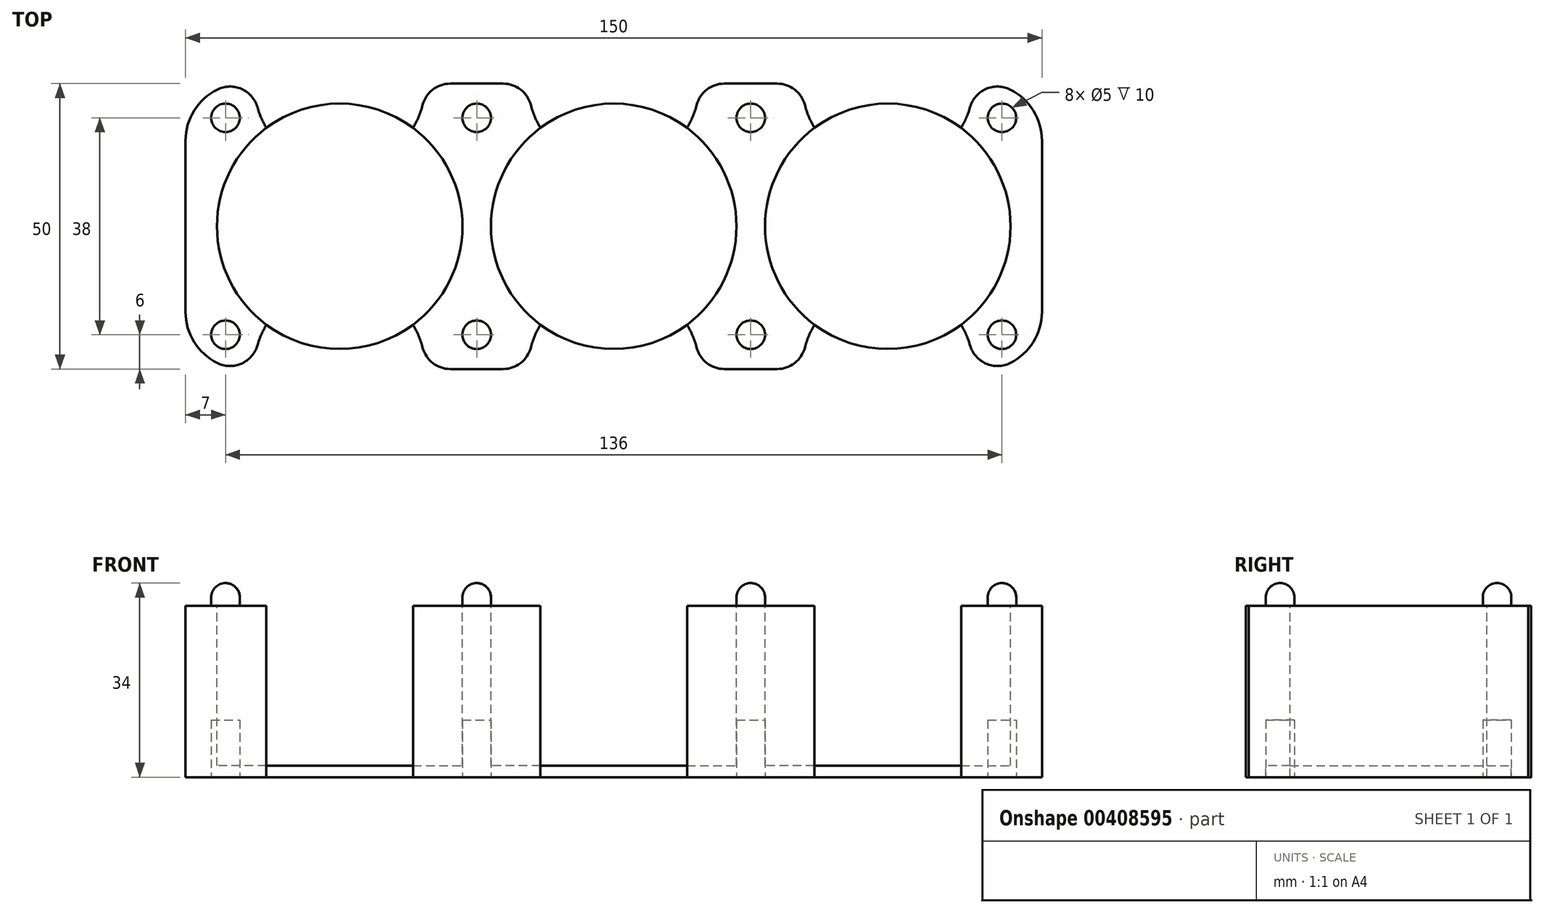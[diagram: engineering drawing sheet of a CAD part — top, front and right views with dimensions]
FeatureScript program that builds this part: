
annotation { "Feature Type Name" : "Feature", "Feature Type Description" : "" }
export const myFeature = defineFeature(function(context is Context, id is Id, definition is map)
    precondition{}
    {
        {
            var Q0;
            Q0=qCreatedBy(makeId("Top.planeOp"),FACE);
            var sketch = newSketch(context, id + "F0", { "sketchPlane" : qUnion([Q0])});
            skLineSegment(sketch, "E0.bottom", {"start": v(0, 0) * mm, "end": v(150, 0) * mm});
            skLineSegment(sketch, "E0.top", {"start": v(0, 50) * mm, "end": v(150, 50) * mm});
            skLineSegment(sketch, "E0.left", {"start": v(0, 0) * mm, "end": v(0, 50) * mm});
            skLineSegment(sketch, "E0.right", {"start": v(150, 0) * mm, "end": v(150, 50) * mm});
            skSolve(sketch);
        }
        {
            var Q0;
            Q0=makeQuery(id+"F0.imprint","IMPRINT",FACE,{"disambiguationData":[TD([[makeQuery(id+"F0.imprint","IMPRINT",EDGE,{"derivedFrom":sQuery(id+"F0.wireOp",EDGE,"E0.bottom")}),1.0]])]});
            var Q1;
            Q1 = qSketchRegion(id + "F2", true);
            extrude(context, id + "F1", {"entities" : qUnion([Q0, Q1]), "depth" : 30 * mm});
        }
        {
            var Q0;
            Q0=makeQuery(id+"F1.opExtrude","CAP_FACE",FACE,{"disambiguationData":[OSD([sQuery(id+"F0.wireOp",EDGE,"E0.bottom"),sQuery(id+"F0.wireOp",EDGE,"E0.top"),sQuery(id+"F0.wireOp",EDGE,"E0.left"),sQuery(id+"F0.wireOp",EDGE,"E0.right")])],"isStart":false});
            var sketch = newSketch(context, id + "F2", { "sketchPlane" : qUnion([Q0])});
            skCircle(sketch, "E1", {"center": v(27, 25) * mm, "radius": 21.5 * mm});
            skCircle(sketch, "E2", {"center": v(75, 25) * mm, "radius": 21.5 * mm});
            skCircle(sketch, "E3", {"center": v(123, 25) * mm, "radius": 21.5 * mm});
            skSolve(sketch);
        }
        {
            var Q0;
            Q0=makeQuery(id+"F2.imprint","IMPRINT",FACE,{"disambiguationData":[TD([[makeQuery(id+"F2.imprint","IMPRINT",EDGE,{"derivedFrom":sQuery(id+"F2.wireOp",EDGE,"E2")}),1.0]])]});
            var Q1;
            Q1=makeQuery(id+"F2.imprint","IMPRINT",FACE,{"disambiguationData":[TD([[makeQuery(id+"F2.imprint","IMPRINT",EDGE,{"derivedFrom":sQuery(id+"F2.wireOp",EDGE,"E3")}),1.0]])]});
            var Q2;
            Q2=makeQuery(id+"F2.imprint","IMPRINT",FACE,{"disambiguationData":[TD([[makeQuery(id+"F2.imprint","IMPRINT",EDGE,{"derivedFrom":sQuery(id+"F2.wireOp",EDGE,"E1")}),1.0]])]});
            extrude(context, id + "F3", {"entities" : qUnion([Q0, Q1, Q2]), "operationType" : NewBodyOperationType.REMOVE, "oppositeDirection" : true, "depth" : 28 * mm});
        }
        {
            var Q0;
            Q0=makeQuery(id+"F1.opExtrude","CAP_FACE",FACE,{"disambiguationData":[OSD([sQuery(id+"F0.wireOp",EDGE,"E0.bottom"),sQuery(id+"F0.wireOp",EDGE,"E0.top"),sQuery(id+"F0.wireOp",EDGE,"E0.left"),sQuery(id+"F0.wireOp",EDGE,"E0.right")])],"isStart":false});
            var sketch = newSketch(context, id + "F4", { "sketchPlane" : qUnion([Q0])});
            skCircle(sketch, "E4", {"center": v(75, 50) * mm, "radius": 15 * mm});
            skCircle(sketch, "E5", {"center": v(123, 50) * mm, "radius": 15 * mm});
            skCircle(sketch, "E6", {"center": v(27, 50) * mm, "radius": 15 * mm});
            skCircle(sketch, "E7", {"center": v(27, 0) * mm, "radius": 15 * mm});
            skCircle(sketch, "E8", {"center": v(75, 0) * mm, "radius": 15 * mm});
            skCircle(sketch, "E9", {"center": v(123, 0) * mm, "radius": 15 * mm});
            skSolve(sketch);
        }
        {
            var Q0;
            {var subQ0=sQuery(id+"F4.wireOp",EDGE,"E4");var subQ1=makeQuery(id+"F1.opExtrude","CAP_EDGE",EDGE,{"disambiguationData":[OSD([sQuery(id+"F0.wireOp",EDGE,"E0.top")])],"isStart":false});var subQ2=makeQuery(id+"F4.imprint","INTERSECT",VERTEX,{"disambiguationData":[OD(0.0)],"derivedFrom":[subQ1,subQ0]});Q0=makeQuery(id+"F4.imprint","IMPRINT",FACE,{"disambiguationData":[TD([[makeQuery(id+"F4.imprint","IMPRINT",EDGE,{"disambiguationData":[TD([[subQ2,1.0]])],"derivedFrom":subQ0}),1.0]])]});}
            var Q1;
            {var subQ0=sQuery(id+"F4.wireOp",EDGE,"E5");var subQ1=makeQuery(id+"F1.opExtrude","CAP_EDGE",EDGE,{"disambiguationData":[OSD([sQuery(id+"F0.wireOp",EDGE,"E0.top")])],"isStart":false});var subQ2=makeQuery(id+"F4.imprint","INTERSECT",VERTEX,{"disambiguationData":[OD(0.0)],"derivedFrom":[subQ1,subQ0]});Q1=makeQuery(id+"F4.imprint","IMPRINT",FACE,{"disambiguationData":[TD([[makeQuery(id+"F4.imprint","IMPRINT",EDGE,{"disambiguationData":[TD([[subQ2,1.0]])],"derivedFrom":subQ0}),1.0]])]});}
            var Q2;
            {var subQ0=sQuery(id+"F4.wireOp",EDGE,"E7");var subQ1=makeQuery(id+"F1.opExtrude","CAP_EDGE",EDGE,{"disambiguationData":[OSD([sQuery(id+"F0.wireOp",EDGE,"E0.bottom")])],"isStart":false});var subQ2=makeQuery(id+"F4.imprint","INTERSECT",VERTEX,{"disambiguationData":[OD(0.0)],"derivedFrom":[subQ1,subQ0]});Q2=makeQuery(id+"F4.imprint","IMPRINT",FACE,{"disambiguationData":[TD([[makeQuery(id+"F4.imprint","IMPRINT",EDGE,{"disambiguationData":[TD([[subQ2,1.0]])],"derivedFrom":subQ0}),1.0]])]});}
            var Q3;
            {var subQ0=sQuery(id+"F4.wireOp",EDGE,"E8");var subQ1=makeQuery(id+"F1.opExtrude","CAP_EDGE",EDGE,{"disambiguationData":[OSD([sQuery(id+"F0.wireOp",EDGE,"E0.bottom")])],"isStart":false});var subQ2=makeQuery(id+"F4.imprint","INTERSECT",VERTEX,{"disambiguationData":[OD(0.0)],"derivedFrom":[subQ1,subQ0]});Q3=makeQuery(id+"F4.imprint","IMPRINT",FACE,{"disambiguationData":[TD([[makeQuery(id+"F4.imprint","IMPRINT",EDGE,{"disambiguationData":[TD([[subQ2,1.0]])],"derivedFrom":subQ0}),1.0]])]});}
            var Q4;
            {var subQ0=sQuery(id+"F4.wireOp",EDGE,"E9");var subQ1=makeQuery(id+"F1.opExtrude","CAP_EDGE",EDGE,{"disambiguationData":[OSD([sQuery(id+"F0.wireOp",EDGE,"E0.bottom")])],"isStart":false});var subQ2=makeQuery(id+"F4.imprint","INTERSECT",VERTEX,{"disambiguationData":[OD(0.0)],"derivedFrom":[subQ1,subQ0]});Q4=makeQuery(id+"F4.imprint","IMPRINT",FACE,{"disambiguationData":[TD([[makeQuery(id+"F4.imprint","IMPRINT",EDGE,{"disambiguationData":[TD([[subQ2,1.0]])],"derivedFrom":subQ0}),1.0]])]});}
            var Q5;
            {var subQ0=sQuery(id+"F4.wireOp",EDGE,"E4");var subQ1=makeQuery(id+"F3.boolean.opBoolean","COPY",EDGE,{"derivedFrom":makeQuery(id+"F3.opExtrude","CAP_EDGE",EDGE,{"disambiguationData":[OSD([sQuery(id+"F2.wireOp",EDGE,"E2")])],"isStart":true})});var subQ2=makeQuery(id+"F4.imprint","INTERSECT",VERTEX,{"disambiguationData":[OD(0.0)],"derivedFrom":[subQ1,subQ0]});Q5=makeQuery(id+"F4.imprint","IMPRINT",FACE,{"disambiguationData":[TD([[makeQuery(id+"F4.imprint","IMPRINT",EDGE,{"disambiguationData":[TD([[subQ2,-1.0]])],"derivedFrom":subQ0}),1.0]])]});}
            var Q6;
            {var subQ0=sQuery(id+"F4.wireOp",EDGE,"E5");var subQ1=makeQuery(id+"F3.boolean.opBoolean","COPY",EDGE,{"derivedFrom":makeQuery(id+"F3.opExtrude","CAP_EDGE",EDGE,{"disambiguationData":[OSD([sQuery(id+"F2.wireOp",EDGE,"E3")])],"isStart":true})});var subQ2=makeQuery(id+"F4.imprint","INTERSECT",VERTEX,{"disambiguationData":[OD(0.0)],"derivedFrom":[subQ1,subQ0]});Q6=makeQuery(id+"F4.imprint","IMPRINT",FACE,{"disambiguationData":[TD([[makeQuery(id+"F4.imprint","IMPRINT",EDGE,{"disambiguationData":[TD([[subQ2,-1.0]])],"derivedFrom":subQ0}),1.0]])]});}
            var Q7;
            {var subQ0=sQuery(id+"F4.wireOp",EDGE,"E6");var subQ1=makeQuery(id+"F3.boolean.opBoolean","COPY",EDGE,{"derivedFrom":makeQuery(id+"F3.opExtrude","CAP_EDGE",EDGE,{"disambiguationData":[OSD([sQuery(id+"F2.wireOp",EDGE,"E1")])],"isStart":true})});var subQ2=makeQuery(id+"F4.imprint","INTERSECT",VERTEX,{"disambiguationData":[OD(0.0)],"derivedFrom":[subQ1,subQ0]});Q7=makeQuery(id+"F4.imprint","IMPRINT",FACE,{"disambiguationData":[TD([[makeQuery(id+"F4.imprint","IMPRINT",EDGE,{"disambiguationData":[TD([[subQ2,-1.0]])],"derivedFrom":subQ0}),1.0]])]});}
            var Q8;
            {var subQ0=sQuery(id+"F4.wireOp",EDGE,"E7");var subQ1=makeQuery(id+"F3.boolean.opBoolean","COPY",EDGE,{"derivedFrom":makeQuery(id+"F3.opExtrude","CAP_EDGE",EDGE,{"disambiguationData":[OSD([sQuery(id+"F2.wireOp",EDGE,"E1")])],"isStart":true})});var subQ2=makeQuery(id+"F4.imprint","INTERSECT",VERTEX,{"disambiguationData":[OD(0.0)],"derivedFrom":[subQ1,subQ0]});Q8=makeQuery(id+"F4.imprint","IMPRINT",FACE,{"disambiguationData":[TD([[makeQuery(id+"F4.imprint","IMPRINT",EDGE,{"disambiguationData":[TD([[subQ2,-1.0]])],"derivedFrom":subQ0}),1.0]])]});}
            var Q9;
            {var subQ0=sQuery(id+"F4.wireOp",EDGE,"E8");var subQ1=makeQuery(id+"F3.boolean.opBoolean","COPY",EDGE,{"derivedFrom":makeQuery(id+"F3.opExtrude","CAP_EDGE",EDGE,{"disambiguationData":[OSD([sQuery(id+"F2.wireOp",EDGE,"E2")])],"isStart":true})});var subQ2=makeQuery(id+"F4.imprint","INTERSECT",VERTEX,{"disambiguationData":[OD(0.0)],"derivedFrom":[subQ1,subQ0]});Q9=makeQuery(id+"F4.imprint","IMPRINT",FACE,{"disambiguationData":[TD([[makeQuery(id+"F4.imprint","IMPRINT",EDGE,{"disambiguationData":[TD([[subQ2,-1.0]])],"derivedFrom":subQ0}),1.0]])]});}
            var Q10;
            {var subQ0=sQuery(id+"F4.wireOp",EDGE,"E9");var subQ1=makeQuery(id+"F3.boolean.opBoolean","COPY",EDGE,{"derivedFrom":makeQuery(id+"F3.opExtrude","CAP_EDGE",EDGE,{"disambiguationData":[OSD([sQuery(id+"F2.wireOp",EDGE,"E3")])],"isStart":true})});var subQ2=makeQuery(id+"F4.imprint","INTERSECT",VERTEX,{"disambiguationData":[OD(0.0)],"derivedFrom":[subQ1,subQ0]});Q10=makeQuery(id+"F4.imprint","IMPRINT",FACE,{"disambiguationData":[TD([[makeQuery(id+"F4.imprint","IMPRINT",EDGE,{"disambiguationData":[TD([[subQ2,-1.0]])],"derivedFrom":subQ0}),1.0]])]});}
            var Q11;
            {var subQ0=sQuery(id+"F4.wireOp",EDGE,"E4");var subQ1=makeQuery(id+"F1.opExtrude","CAP_EDGE",EDGE,{"disambiguationData":[OSD([sQuery(id+"F0.wireOp",EDGE,"E0.top")])],"isStart":false});var subQ2=makeQuery(id+"F4.imprint","INTERSECT",VERTEX,{"disambiguationData":[OD(0.0)],"derivedFrom":[subQ1,subQ0]});Q11=makeQuery(id+"F4.imprint","IMPRINT",FACE,{"disambiguationData":[TD([[makeQuery(id+"F4.imprint","IMPRINT",EDGE,{"disambiguationData":[TD([[subQ2,-1.0]])],"derivedFrom":subQ0}),1.0]])]});}
            var Q12;
            {var subQ0=sQuery(id+"F4.wireOp",EDGE,"E5");var subQ1=makeQuery(id+"F1.opExtrude","CAP_EDGE",EDGE,{"disambiguationData":[OSD([sQuery(id+"F0.wireOp",EDGE,"E0.top")])],"isStart":false});var subQ2=makeQuery(id+"F4.imprint","INTERSECT",VERTEX,{"disambiguationData":[OD(0.0)],"derivedFrom":[subQ1,subQ0]});Q12=makeQuery(id+"F4.imprint","IMPRINT",FACE,{"disambiguationData":[TD([[makeQuery(id+"F4.imprint","IMPRINT",EDGE,{"disambiguationData":[TD([[subQ2,-1.0]])],"derivedFrom":subQ0}),1.0]])]});}
            var Q13;
            {var subQ0=sQuery(id+"F4.wireOp",EDGE,"E6");var subQ1=makeQuery(id+"F1.opExtrude","CAP_EDGE",EDGE,{"disambiguationData":[OSD([sQuery(id+"F0.wireOp",EDGE,"E0.top")])],"isStart":false});var subQ2=makeQuery(id+"F4.imprint","INTERSECT",VERTEX,{"disambiguationData":[OD(0.0)],"derivedFrom":[subQ1,subQ0]});Q13=makeQuery(id+"F4.imprint","IMPRINT",FACE,{"disambiguationData":[TD([[makeQuery(id+"F4.imprint","IMPRINT",EDGE,{"disambiguationData":[TD([[subQ2,-1.0]])],"derivedFrom":subQ0}),1.0]])]});}
            var Q14;
            {var subQ0=sQuery(id+"F4.wireOp",EDGE,"E7");var subQ1=makeQuery(id+"F1.opExtrude","CAP_EDGE",EDGE,{"disambiguationData":[OSD([sQuery(id+"F0.wireOp",EDGE,"E0.bottom")])],"isStart":false});var subQ2=makeQuery(id+"F4.imprint","INTERSECT",VERTEX,{"disambiguationData":[OD(0.0)],"derivedFrom":[subQ1,subQ0]});Q14=makeQuery(id+"F4.imprint","IMPRINT",FACE,{"disambiguationData":[TD([[makeQuery(id+"F4.imprint","IMPRINT",EDGE,{"disambiguationData":[TD([[subQ2,-1.0]])],"derivedFrom":subQ0}),1.0]])]});}
            var Q15;
            {var subQ0=sQuery(id+"F4.wireOp",EDGE,"E8");var subQ1=makeQuery(id+"F1.opExtrude","CAP_EDGE",EDGE,{"disambiguationData":[OSD([sQuery(id+"F0.wireOp",EDGE,"E0.bottom")])],"isStart":false});var subQ2=makeQuery(id+"F4.imprint","INTERSECT",VERTEX,{"disambiguationData":[OD(0.0)],"derivedFrom":[subQ1,subQ0]});Q15=makeQuery(id+"F4.imprint","IMPRINT",FACE,{"disambiguationData":[TD([[makeQuery(id+"F4.imprint","IMPRINT",EDGE,{"disambiguationData":[TD([[subQ2,-1.0]])],"derivedFrom":subQ0}),1.0]])]});}
            var Q16;
            {var subQ0=sQuery(id+"F4.wireOp",EDGE,"E9");var subQ1=makeQuery(id+"F1.opExtrude","CAP_EDGE",EDGE,{"disambiguationData":[OSD([sQuery(id+"F0.wireOp",EDGE,"E0.bottom")])],"isStart":false});var subQ2=makeQuery(id+"F4.imprint","INTERSECT",VERTEX,{"disambiguationData":[OD(0.0)],"derivedFrom":[subQ1,subQ0]});Q16=makeQuery(id+"F4.imprint","IMPRINT",FACE,{"disambiguationData":[TD([[makeQuery(id+"F4.imprint","IMPRINT",EDGE,{"disambiguationData":[TD([[subQ2,-1.0]])],"derivedFrom":subQ0}),1.0]])]});}
            extrude(context, id + "F5", {"entities" : qUnion([Q0, Q1, Q2, Q3, Q4, Q5, Q6, Q7, Q8, Q9, Q10, Q11, Q12, Q13, Q14, Q15, Q16]), "operationType" : NewBodyOperationType.REMOVE, "endBound" : BoundingType.THROUGH_ALL, "oppositeDirection" : true, "depth" : 25 * mm});
        }
        {
            var Q0;
            Q0=makeQuery(id+"F1.opExtrude","SWEPT_EDGE",EDGE,{"disambiguationData":[OSD([sQuery(id+"F0.wireOp",EDGE,"E0.bottom"),sQuery(id+"F0.wireOp",EDGE,"E0.right")])]});
            fillet(context, id + "F6", {"entities" : qUnion([Q0]), "radius" : 10 * mm, "tangentPropagation" : true, "allowEdgeOverflow" : false});
        }
        {
            var Q0;
            Q0=makeQuery(id+"F1.opExtrude","SWEPT_EDGE",EDGE,{"disambiguationData":[OSD([sQuery(id+"F0.wireOp",EDGE,"E0.top"),sQuery(id+"F0.wireOp",EDGE,"E0.right")])]});
            var Q1;
            Q1=makeQuery(id+"F1.opExtrude","SWEPT_EDGE",EDGE,{"disambiguationData":[OSD([sQuery(id+"F0.wireOp",EDGE,"E0.bottom"),sQuery(id+"F0.wireOp",EDGE,"E0.left")])]});
            var Q2;
            Q2=makeQuery(id+"F1.opExtrude","SWEPT_EDGE",EDGE,{"disambiguationData":[OSD([sQuery(id+"F0.wireOp",EDGE,"E0.top"),sQuery(id+"F0.wireOp",EDGE,"E0.left")])]});
            fillet(context, id + "F7", {"entities" : qUnion([Q0, Q1, Q2]), "radius" : 10 * mm, "tangentPropagation" : true, "allowEdgeOverflow" : false});
        }
        {
            var Q0;
            Q0=makeQuery(id+"F5.boolean.opBoolean","INTERSECT",EDGE,{"disambiguationData":[OD(0.0)],"derivedFrom":[makeQuery(id+"F1.opExtrude","SWEPT_FACE",FACE,{"disambiguationData":[OSD([sQuery(id+"F0.wireOp",EDGE,"E0.bottom")])]}),makeQuery(id+"F5.opExtrude","SWEPT_FACE",FACE,{"disambiguationData":[OSD([sQuery(id+"F4.wireOp",EDGE,"E7")])]})]});
            var Q1;
            {var subQ0=sQuery(id+"F4.wireOp",EDGE,"E6");var subQ1=sQuery(id+"F0.wireOp",EDGE,"E0.top");Q1=makeQuery(id+"F5.boolean.opBoolean","COPY",EDGE,{"derivedFrom":makeQuery(id+"F5.opExtrude","SWEPT_EDGE",EDGE,{"disambiguationData":[OSD([subQ1,subQ0]),TDD([makeQuery(id+"F4.imprint","INTERSECT",VERTEX,{"disambiguationData":[OD(0.0)],"derivedFrom":[makeQuery(id+"F1.opExtrude","CAP_EDGE",EDGE,{"disambiguationData":[OSD([subQ1])],"isStart":false}),subQ0]})])]})});}
            var Q2;
            Q2=makeQuery(id+"F5.boolean.opBoolean","INTERSECT",EDGE,{"disambiguationData":[OD(0.0)],"derivedFrom":[makeQuery(id+"F1.opExtrude","SWEPT_FACE",FACE,{"disambiguationData":[OSD([sQuery(id+"F0.wireOp",EDGE,"E0.top")])]}),makeQuery(id+"F5.opExtrude","SWEPT_FACE",FACE,{"disambiguationData":[OSD([sQuery(id+"F4.wireOp",EDGE,"E4")])]})]});
            var Q3;
            Q3=makeQuery(id+"F5.boolean.opBoolean","INTERSECT",EDGE,{"disambiguationData":[OD(1.0)],"derivedFrom":[makeQuery(id+"F1.opExtrude","SWEPT_FACE",FACE,{"disambiguationData":[OSD([sQuery(id+"F0.wireOp",EDGE,"E0.top")])]}),makeQuery(id+"F5.opExtrude","SWEPT_FACE",FACE,{"disambiguationData":[OSD([sQuery(id+"F4.wireOp",EDGE,"E5")])]})]});
            var Q4;
            Q4=makeQuery(id+"F5.boolean.opBoolean","INTERSECT",EDGE,{"disambiguationData":[OD(1.0)],"derivedFrom":[makeQuery(id+"F1.opExtrude","SWEPT_FACE",FACE,{"disambiguationData":[OSD([sQuery(id+"F0.wireOp",EDGE,"E0.bottom")])]}),makeQuery(id+"F5.opExtrude","SWEPT_FACE",FACE,{"disambiguationData":[OSD([sQuery(id+"F4.wireOp",EDGE,"E9")])]})]});
            var Q5;
            Q5=makeQuery(id+"F5.boolean.opBoolean","INTERSECT",EDGE,{"disambiguationData":[OD(1.0)],"derivedFrom":[makeQuery(id+"F1.opExtrude","SWEPT_FACE",FACE,{"disambiguationData":[OSD([sQuery(id+"F0.wireOp",EDGE,"E0.bottom")])]}),makeQuery(id+"F5.opExtrude","SWEPT_FACE",FACE,{"disambiguationData":[OSD([sQuery(id+"F4.wireOp",EDGE,"E8")])]})]});
            var Q6;
            Q6=makeQuery(id+"F5.boolean.opBoolean","INTERSECT",EDGE,{"disambiguationData":[OD(1.0)],"derivedFrom":[makeQuery(id+"F1.opExtrude","SWEPT_FACE",FACE,{"disambiguationData":[OSD([sQuery(id+"F0.wireOp",EDGE,"E0.bottom")])]}),makeQuery(id+"F5.opExtrude","SWEPT_FACE",FACE,{"disambiguationData":[OSD([sQuery(id+"F4.wireOp",EDGE,"E7")])]})]});
            var Q7;
            Q7=makeQuery(id+"F5.boolean.opBoolean","INTERSECT",EDGE,{"disambiguationData":[OD(0.0)],"derivedFrom":[makeQuery(id+"F1.opExtrude","SWEPT_FACE",FACE,{"disambiguationData":[OSD([sQuery(id+"F0.wireOp",EDGE,"E0.bottom")])]}),makeQuery(id+"F5.opExtrude","SWEPT_FACE",FACE,{"disambiguationData":[OSD([sQuery(id+"F4.wireOp",EDGE,"E8")])]})]});
            var Q8;
            Q8=makeQuery(id+"F5.boolean.opBoolean","INTERSECT",EDGE,{"disambiguationData":[OD(0.0)],"derivedFrom":[makeQuery(id+"F1.opExtrude","SWEPT_FACE",FACE,{"disambiguationData":[OSD([sQuery(id+"F0.wireOp",EDGE,"E0.bottom")])]}),makeQuery(id+"F5.opExtrude","SWEPT_FACE",FACE,{"disambiguationData":[OSD([sQuery(id+"F4.wireOp",EDGE,"E9")])]})]});
            var Q9;
            {var subQ0=sQuery(id+"F4.wireOp",EDGE,"E6");var subQ1=sQuery(id+"F0.wireOp",EDGE,"E0.top");Q9=makeQuery(id+"F5.boolean.opBoolean","COPY",EDGE,{"derivedFrom":makeQuery(id+"F5.opExtrude","SWEPT_EDGE",EDGE,{"disambiguationData":[OSD([subQ1,subQ0]),TDD([makeQuery(id+"F4.imprint","INTERSECT",VERTEX,{"disambiguationData":[OD(1.0)],"derivedFrom":[makeQuery(id+"F1.opExtrude","CAP_EDGE",EDGE,{"disambiguationData":[OSD([subQ1])],"isStart":false}),subQ0]})])]})});}
            var Q10;
            Q10=makeQuery(id+"F5.boolean.opBoolean","INTERSECT",EDGE,{"disambiguationData":[OD(1.0)],"derivedFrom":[makeQuery(id+"F1.opExtrude","SWEPT_FACE",FACE,{"disambiguationData":[OSD([sQuery(id+"F0.wireOp",EDGE,"E0.top")])]}),makeQuery(id+"F5.opExtrude","SWEPT_FACE",FACE,{"disambiguationData":[OSD([sQuery(id+"F4.wireOp",EDGE,"E4")])]})]});
            var Q11;
            Q11=makeQuery(id+"F5.boolean.opBoolean","INTERSECT",EDGE,{"disambiguationData":[OD(0.0)],"derivedFrom":[makeQuery(id+"F1.opExtrude","SWEPT_FACE",FACE,{"disambiguationData":[OSD([sQuery(id+"F0.wireOp",EDGE,"E0.top")])]}),makeQuery(id+"F5.opExtrude","SWEPT_FACE",FACE,{"disambiguationData":[OSD([sQuery(id+"F4.wireOp",EDGE,"E5")])]})]});
            fillet(context, id + "F8", {"entities" : qUnion([Q0, Q1, Q2, Q3, Q4, Q5, Q6, Q7, Q8, Q9, Q10, Q11]), "radius" : 5 * mm, "tangentPropagation" : true, "allowEdgeOverflow" : false});
        }
        {
            var Q0;
            {var subQ0=sQuery(id+"F0.wireOp",EDGE,"E0.bottom");var subQ1=sQuery(id+"F0.wireOp",EDGE,"E0.top");Q0=makeQuery(id+"F5.boolean.opBoolean","SPLIT",FACE,{"disambiguationData":[TD([makeQuery(id+"F1.opExtrude","SWEPT_FACE",FACE,{"disambiguationData":[OSD([subQ0])]}),makeQuery(id+"F1.opExtrude","SWEPT_FACE",FACE,{"disambiguationData":[OSD([subQ1])]}),makeQuery(id+"F3.boolean.opBoolean","COPY",FACE,{"derivedFrom":makeQuery(id+"F3.opExtrude","SWEPT_FACE",FACE,{"disambiguationData":[OSD([sQuery(id+"F2.wireOp",EDGE,"E1")])]})}),makeQuery(id+"F3.boolean.opBoolean","COPY",FACE,{"derivedFrom":makeQuery(id+"F3.opExtrude","SWEPT_FACE",FACE,{"disambiguationData":[OSD([sQuery(id+"F2.wireOp",EDGE,"E2")])]})}),makeQuery(id+"F5.opExtrude","SWEPT_FACE",FACE,{"disambiguationData":[OSD([sQuery(id+"F4.wireOp",EDGE,"E4")])]}),makeQuery(id+"F5.opExtrude","SWEPT_FACE",FACE,{"disambiguationData":[OSD([sQuery(id+"F4.wireOp",EDGE,"E6")])]}),makeQuery(id+"F5.opExtrude","SWEPT_FACE",FACE,{"disambiguationData":[OSD([sQuery(id+"F4.wireOp",EDGE,"E7")])]}),makeQuery(id+"F5.opExtrude","SWEPT_FACE",FACE,{"disambiguationData":[OSD([sQuery(id+"F4.wireOp",EDGE,"E8")])]})])],"derivedFrom":makeQuery(id+"F1.opExtrude","CAP_FACE",FACE,{"disambiguationData":[OSD([subQ0,subQ1,sQuery(id+"F0.wireOp",EDGE,"E0.left"),sQuery(id+"F0.wireOp",EDGE,"E0.right")])],"isStart":false})});}
            var sketch = newSketch(context, id + "F9", { "sketchPlane" : qUnion([Q0])});
            skCircle(sketch, "E10", {"center": v(7, 44) * mm, "radius": 2.5 * mm});
            skCircle(sketch, "E11", {"center": v(51, 44) * mm, "radius": 2.5 * mm});
            skPoint(sketch, "E12.centerSnap0", {"position": v(61.17, 44.19) * mm});
            skCircle(sketch, "E13", {"center": v(143, 44) * mm, "radius": 2.5 * mm});
            skCircle(sketch, "E14", {"center": v(7, 6) * mm, "radius": 2.5 * mm});
            skCircle(sketch, "E15", {"center": v(51, 6) * mm, "radius": 2.5 * mm});
            skCircle(sketch, "E16", {"center": v(99, 6) * mm, "radius": 2.5 * mm});
            skCircle(sketch, "E17", {"center": v(143, 6) * mm, "radius": 2.5 * mm});
            skCircle(sketch, "E18", {"center": v(99, 44) * mm, "radius": 2.5 * mm});
            skSolve(sketch);
        }
        {
            var Q0;
            Q0 = qSketchRegion(id + "F9", true);
            extrude(context, id + "F10", {"entities" : qUnion([Q0]), "operationType" : NewBodyOperationType.ADD, "depth" : 4 * mm});
        }
        {
            var Q0;
            Q0=makeQuery(id+"F10.opExtrude","CAP_EDGE",EDGE,{"disambiguationData":[OSD([sQuery(id+"F9.wireOp",EDGE,"E14")])],"isStart":false});
            var Q1;
            Q1=makeQuery(id+"F10.opExtrude","CAP_EDGE",EDGE,{"disambiguationData":[OSD([sQuery(id+"F9.wireOp",EDGE,"E10")])],"isStart":false});
            var Q2;
            Q2=makeQuery(id+"F10.opExtrude","CAP_EDGE",EDGE,{"disambiguationData":[OSD([sQuery(id+"F9.wireOp",EDGE,"E15")])],"isStart":false});
            var Q3;
            Q3=makeQuery(id+"F10.opExtrude","CAP_EDGE",EDGE,{"disambiguationData":[OSD([sQuery(id+"F9.wireOp",EDGE,"E11")])],"isStart":false});
            var Q4;
            Q4=makeQuery(id+"F10.opExtrude","CAP_EDGE",EDGE,{"disambiguationData":[OSD([sQuery(id+"F9.wireOp",EDGE,"E18")])],"isStart":false});
            var Q5;
            Q5=makeQuery(id+"F10.opExtrude","CAP_EDGE",EDGE,{"disambiguationData":[OSD([sQuery(id+"F9.wireOp",EDGE,"E16")])],"isStart":false});
            var Q6;
            Q6=makeQuery(id+"F10.opExtrude","CAP_EDGE",EDGE,{"disambiguationData":[OSD([sQuery(id+"F9.wireOp",EDGE,"E17")])],"isStart":false});
            var Q7;
            Q7=makeQuery(id+"F10.opExtrude","CAP_EDGE",EDGE,{"disambiguationData":[OSD([sQuery(id+"F9.wireOp",EDGE,"E13")])],"isStart":false});
            fillet(context, id + "F11", {"entities" : qUnion([Q0, Q1, Q2, Q3, Q4, Q5, Q6, Q7]), "radius" : 2.5 * mm, "tangentPropagation" : true, "allowEdgeOverflow" : false});
        }
        {
            var Q0;
            Q0=makeQuery(id+"F1.opExtrude","CAP_FACE",FACE,{"disambiguationData":[OSD([sQuery(id+"F0.wireOp",EDGE,"E0.bottom"),sQuery(id+"F0.wireOp",EDGE,"E0.top"),sQuery(id+"F0.wireOp",EDGE,"E0.left"),sQuery(id+"F0.wireOp",EDGE,"E0.right")])],"isStart":true});
            var sketch = newSketch(context, id + "F12", { "sketchPlane" : qUnion([Q0])});
            skCircle(sketch, "E19", {"center": v(7, -6) * mm, "radius": 2.5 * mm});
            skCircle(sketch, "E20", {"center": v(51, -6) * mm, "radius": 2.5 * mm});
            skPoint(sketch, "E21.centerSnap0", {"position": v(126.78, -7.26) * mm});
            skCircle(sketch, "E22", {"center": v(143, -6) * mm, "radius": 2.5 * mm});
            skCircle(sketch, "E23", {"center": v(7, -44) * mm, "radius": 2.5 * mm});
            skCircle(sketch, "E24", {"center": v(51, -44) * mm, "radius": 2.5 * mm});
            skCircle(sketch, "E25", {"center": v(99, -44) * mm, "radius": 2.5 * mm});
            skCircle(sketch, "E26", {"center": v(143, -44) * mm, "radius": 2.5 * mm});
            skCircle(sketch, "E27", {"center": v(99, -6) * mm, "radius": 2.5 * mm});
            skSolve(sketch);
        }
        {
            var Q0;
            Q0=makeQuery(id+"F12.imprint","IMPRINT",FACE,{"disambiguationData":[TD([[makeQuery(id+"F12.imprint","IMPRINT",EDGE,{"derivedFrom":sQuery(id+"F12.wireOp",EDGE,"E19")}),1.0]])]});
            var Q1;
            Q1=makeQuery(id+"F12.imprint","IMPRINT",FACE,{"disambiguationData":[TD([[makeQuery(id+"F12.imprint","IMPRINT",EDGE,{"derivedFrom":sQuery(id+"F12.wireOp",EDGE,"E20")}),1.0]])]});
            var Q2;
            Q2=makeQuery(id+"F12.imprint","IMPRINT",FACE,{"disambiguationData":[TD([[makeQuery(id+"F12.imprint","IMPRINT",EDGE,{"derivedFrom":sQuery(id+"F12.wireOp",EDGE,"E22")}),1.0]])]});
            var Q3;
            Q3=makeQuery(id+"F12.imprint","IMPRINT",FACE,{"disambiguationData":[TD([[makeQuery(id+"F12.imprint","IMPRINT",EDGE,{"derivedFrom":sQuery(id+"F12.wireOp",EDGE,"E23")}),1.0]])]});
            var Q4;
            Q4=makeQuery(id+"F12.imprint","IMPRINT",FACE,{"disambiguationData":[TD([[makeQuery(id+"F12.imprint","IMPRINT",EDGE,{"derivedFrom":sQuery(id+"F12.wireOp",EDGE,"E24")}),1.0]])]});
            var Q5;
            Q5=makeQuery(id+"F12.imprint","IMPRINT",FACE,{"disambiguationData":[TD([[makeQuery(id+"F12.imprint","IMPRINT",EDGE,{"derivedFrom":sQuery(id+"F12.wireOp",EDGE,"E25")}),1.0]])]});
            var Q6;
            Q6=makeQuery(id+"F12.imprint","IMPRINT",FACE,{"disambiguationData":[TD([[makeQuery(id+"F12.imprint","IMPRINT",EDGE,{"derivedFrom":sQuery(id+"F12.wireOp",EDGE,"E27")}),1.0]])]});
            var Q7;
            Q7=makeQuery(id+"F12.imprint","IMPRINT",FACE,{"disambiguationData":[TD([[makeQuery(id+"F12.imprint","IMPRINT",EDGE,{"derivedFrom":sQuery(id+"F12.wireOp",EDGE,"E26")}),1.0]])]});
            extrude(context, id + "F13", {"entities" : qUnion([Q0, Q1, Q2, Q3, Q4, Q5, Q6, Q7]), "operationType" : NewBodyOperationType.REMOVE, "oppositeDirection" : true, "depth" : 10 * mm});
        }
    });
